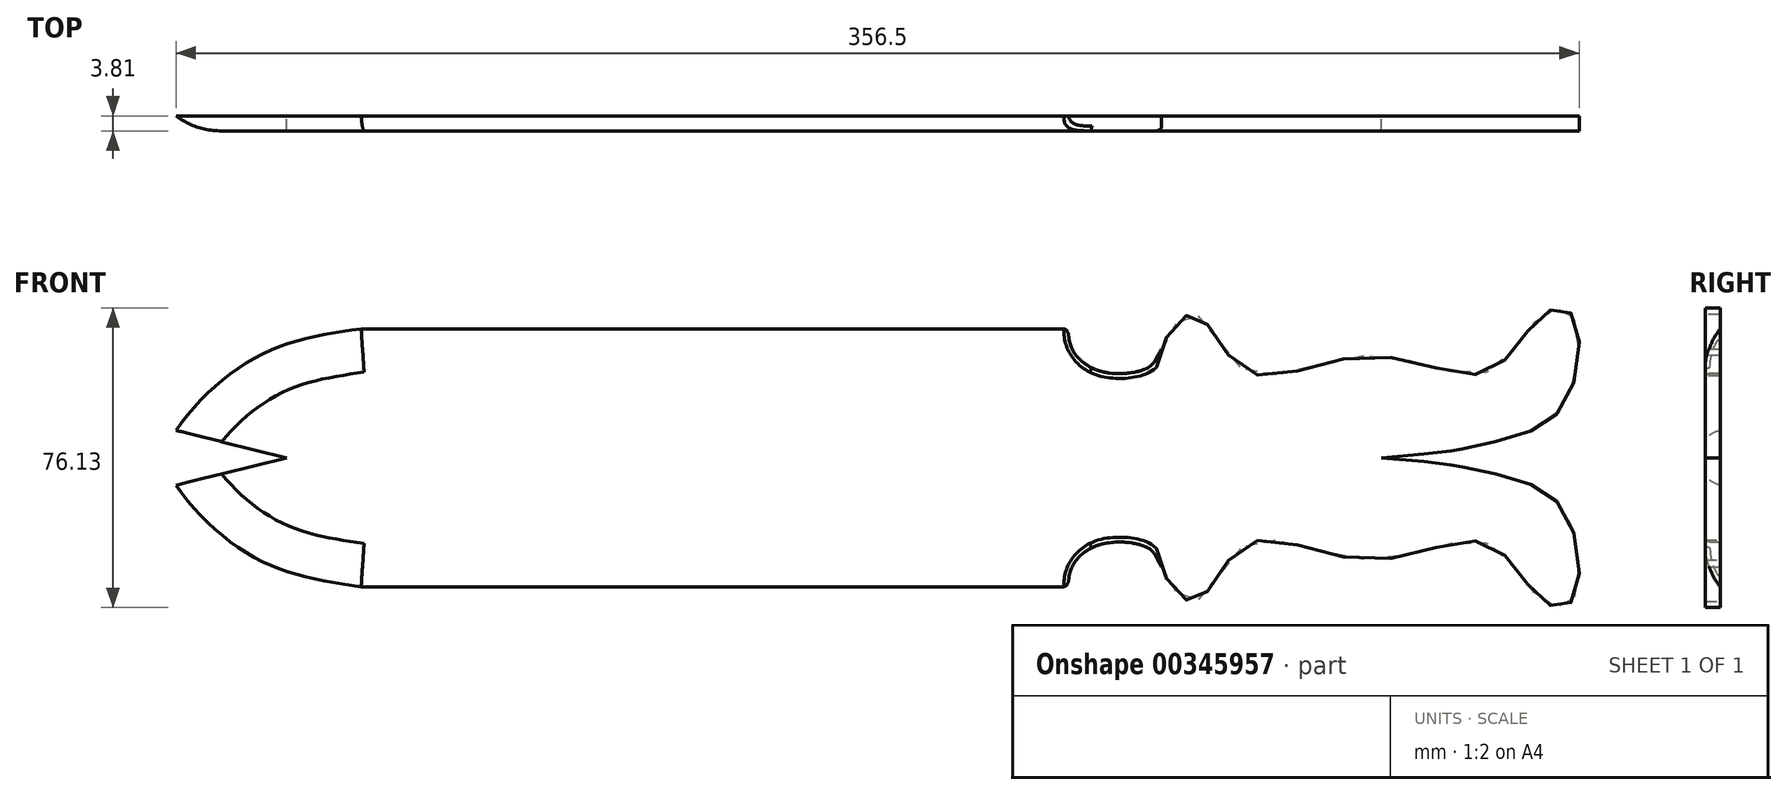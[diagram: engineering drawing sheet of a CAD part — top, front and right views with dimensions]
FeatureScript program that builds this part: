
annotation { "Feature Type Name" : "Feature", "Feature Type Description" : "" }
export const myFeature = defineFeature(function(context is Context, id is Id, definition is map)
    precondition{}
    {
        {
            var Q0;
            Q0=qCreatedBy(makeId("Front.planeOp"),FACE);
            var sketch = newSketch(context, id + "F0", { "sketchPlane" : qUnion([Q0])});
            skLineSegment(sketch, "E0", {"start": v(116.43, 36.37) * mm, "end": v(-140.45, 36.37) * mm});
            skLineSegment(sketch, "E1", {"start": v(-140.45, 36.37) * mm, "end": v(-168.5, 29.4) * mm});
            skFitSpline(sketch, "E2", {"points": [v(116.43, 36.37) * mm, v(137.79, 36.37) * mm, v(155.86, 34.55) * mm, v(156.05, 34.52) * mm, v(170.4, 31.3) * mm, v(184.87, 21.6) * mm, v(186.27, 0) * mm, v(178.7, 0) * mm, v(164.61, 14.62) * mm, v(134.75, 10.43) * mm, v(103.5, 14.44) * mm, v(90.4, 0) * mm, v(81.92, 8.69) * mm], "startDerivative": vector(208.1, 12.43) * mm, "endDerivative": vector(-55.98, 188.94) * mm});
            skFitSpline(sketch, "E3", {"points": [v(81.92, 8.69) * mm, v(78.5, 13.45) * mm, v(66, 14.24) * mm, v(58.3, 3.61) * mm], "startDerivative": vector(-18.13, 30.3) * mm, "endDerivative": vector(3.89, -43.06) * mm});
            skLineSegment(sketch, "E4", {"start": v(58.3, 3.61) * mm, "end": v(-121.46, 3.61) * mm});
            skFitSpline(sketch, "E5", {"points": [v(-168.5, 29.4) * mm, v(-147.02, 10.25) * mm, v(-121.46, 3.61) * mm], "startDerivative": vector(31.96, -46.67) * mm, "endDerivative": vector(55.47, -7.45) * mm});
            skSolve(sketch);
        }
        {
            var Q0;
            Q0=makeQuery(id+"F0.imprint","IMPRINT",FACE,{"disambiguationData":[TD([[makeQuery(id+"F0.imprint","IMPRINT",EDGE,{"derivedFrom":sQuery(id+"F0.wireOp",EDGE,"E0")}),1.0]])]});
            extrude(context, id + "F1", {"entities" : qUnion([Q0]), "depth" : 3.8 * mm});
        }
        {
            var Q0;
            Q0=makeQuery(id+"F1.opExtrude","CAP_EDGE",EDGE,{"disambiguationData":[OSD([sQuery(id+"F0.wireOp",EDGE,"E4")])],"isStart":false});
            var Q1;
            Q1=makeQuery(id+"F1.opExtrude","CAP_EDGE",EDGE,{"disambiguationData":[OSD([sQuery(id+"F0.wireOp",EDGE,"E5")])],"isStart":false});
            fillet(context, id + "F2", {"entities" : qUnion([Q0, Q1]), "radius" : 17.78 * mm, "tangentPropagation" : true, "allowEdgeOverflow" : false});
        }
        {
            var Q0;
            Q0=makeQuery(id+"F1.opExtrude","CAP_EDGE",EDGE,{"disambiguationData":[OSD([sQuery(id+"F0.wireOp",EDGE,"E3")])],"isStart":false});
            fillet(context, id + "F3", {"entities" : qUnion([Q0]), "radius" : 1.23 * mm, "tangentPropagation" : true, "allowEdgeOverflow" : false});
        }
        {
            var Q0;
            Q0=makeQuery(id+"F1.opExtrude","SWEPT_BODY",BODY,{"disambiguationData":[OSD([sQuery(id+"F0.wireOp",EDGE,"E0"),sQuery(id+"F0.wireOp",EDGE,"E1"),sQuery(id+"F0.wireOp",EDGE,"E2"),sQuery(id+"F0.wireOp",EDGE,"E3"),sQuery(id+"F0.wireOp",EDGE,"E4"),sQuery(id+"F0.wireOp",EDGE,"E5")])]});
            var Q1;
            Q1=makeQuery(id+"F1.opExtrude","SWEPT_FACE",FACE,{"disambiguationData":[OSD([sQuery(id+"F0.wireOp",EDGE,"E0")])]});
            mirror(context, id + "F4", {"operationType" : NewBodyOperationType.ADD, "entities" : qUnion([Q0]), "mirrorPlane" : qUnion([Q1])});
        }
    });
